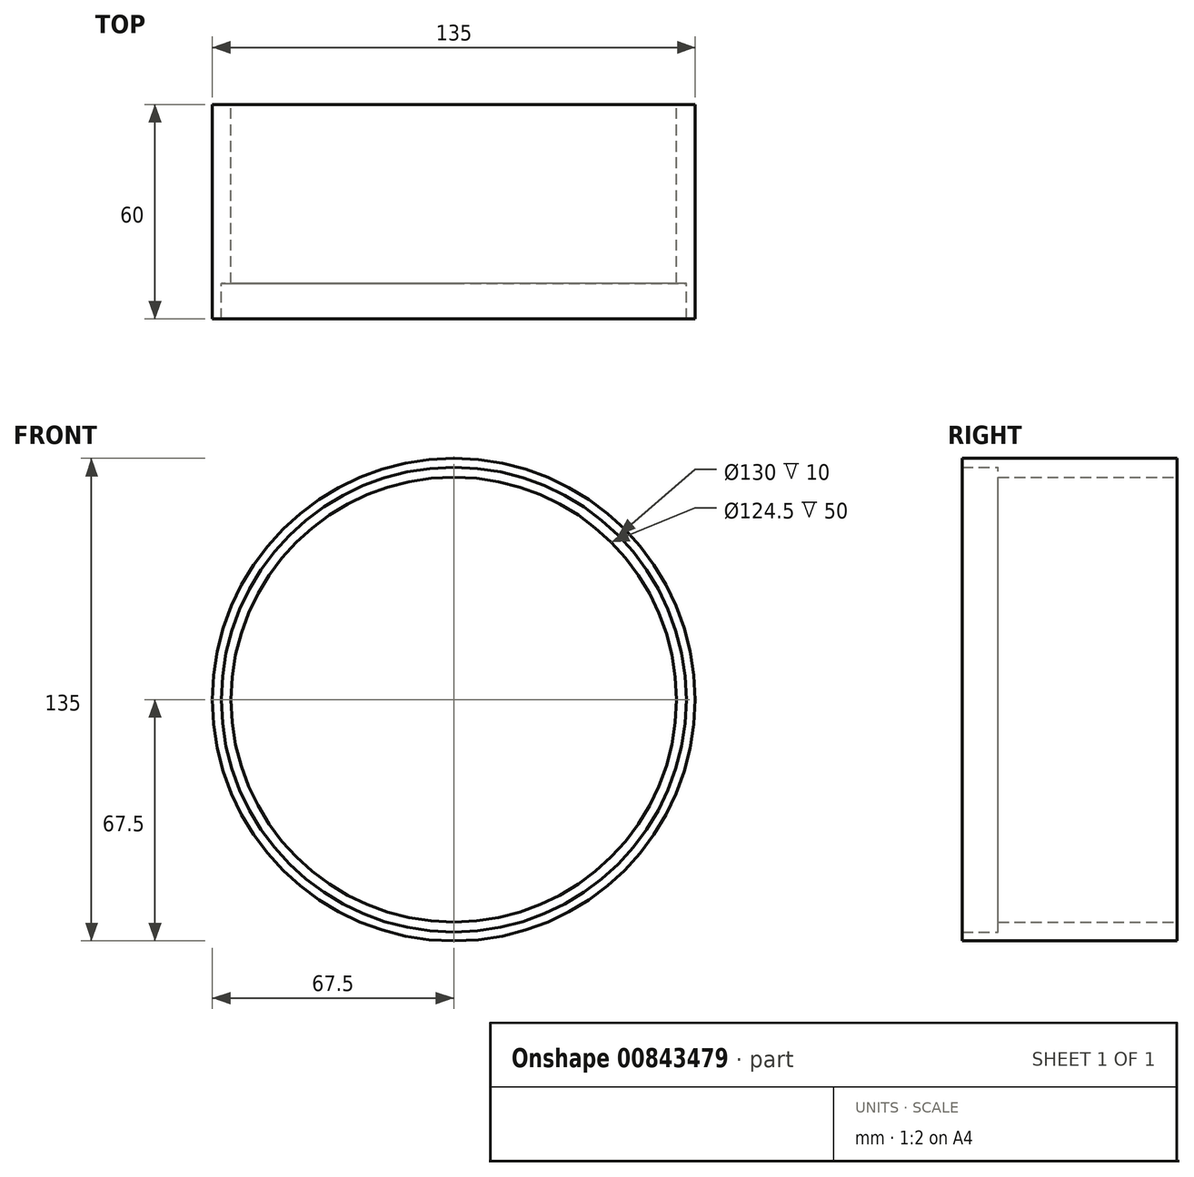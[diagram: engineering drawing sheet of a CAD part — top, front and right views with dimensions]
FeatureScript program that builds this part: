
annotation { "Feature Type Name" : "Feature", "Feature Type Description" : "" }
export const myFeature = defineFeature(function(context is Context, id is Id, definition is map)
    precondition{}
    {
        {
            var Q0;
            Q0=qCreatedBy(makeId("Front.planeOp"),FACE);
            var sketch = newSketch(context, id + "F0", { "sketchPlane" : qUnion([Q0])});
            skCircle(sketch, "E0", {"center": v(0, 0) * mm, "radius": 65 * mm});
            skCircle(sketch, "E1", {"center": v(0, 0) * mm, "radius": 67.5 * mm});
            skSolve(sketch);
        }
        {
            var Q0;
            Q0=makeQuery(id+"F0.imprint","IMPRINT",FACE,{"disambiguationData":[TD([[makeQuery(id+"F0.imprint","IMPRINT",EDGE,{"derivedFrom":sQuery(id+"F0.wireOp",EDGE,"E0")}),-1.0]])]});
            extrude(context, id + "F1", {"entities" : qUnion([Q0]), "depth" : 10 * mm, "offsetDistance" : 25 * mm});
        }
        {
            var Q0;
            Q0=qCreatedBy(makeId("Front.planeOp"),FACE);
            var sketch = newSketch(context, id + "F2", { "sketchPlane" : qUnion([Q0])});
            skCircle(sketch, "E2", {"center": v(0, 0) * mm, "radius": 62.25 * mm});
            skCircle(sketch, "E3", {"center": v(0, 0) * mm, "radius": 67.5 * mm});
            skSolve(sketch);
        }
        {
            var Q0;
            Q0=makeQuery(id+"F1.opExtrude","CAP_FACE",FACE,{"disambiguationData":[OSD([sQuery(id+"F0.wireOp",EDGE,"E0"),sQuery(id+"F0.wireOp",EDGE,"E1")])],"isStart":false});
            var Q1;
            Q1=makeQuery(id+"F2.imprint","IMPRINT",FACE,{"disambiguationData":[TD([[makeQuery(id+"F2.imprint","IMPRINT",EDGE,{"derivedFrom":sQuery(id+"F2.wireOp",EDGE,"E2")}),-1.0]])]});
            extrude(context, id + "F3", {"entities" : qUnion([Q0, Q1]), "operationType" : NewBodyOperationType.ADD, "depth" : 50 * mm, "offsetDistance" : 25 * mm});
        }
    });
